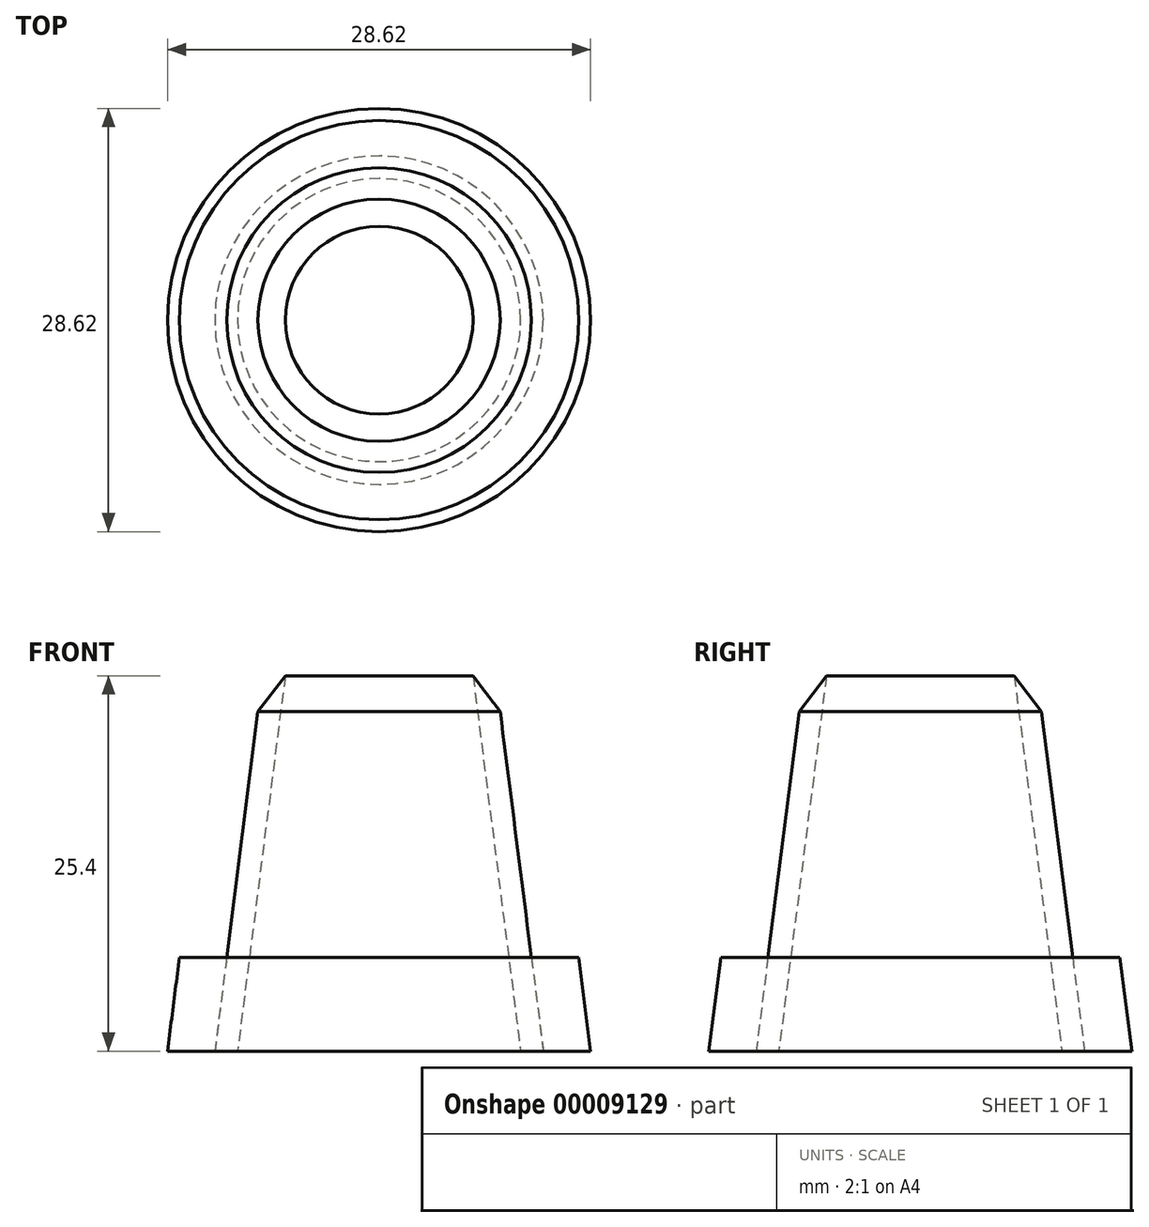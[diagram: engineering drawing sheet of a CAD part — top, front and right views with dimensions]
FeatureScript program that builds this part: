
annotation { "Feature Type Name" : "Feature", "Feature Type Description" : "" }
export const myFeature = defineFeature(function(context is Context, id is Id, definition is map)
    precondition{}
    {
        {
            var Q0;
            Q0=qCreatedBy(makeId("Front.planeOp"),FACE);
            var sketch = newSketch(context, id + "F0", { "sketchPlane" : qUnion([Q0])});
            skLineSegment(sketch, "E0", {"start": v(-11.11, 0) * mm, "end": v(-8.2, 22.97) * mm});
            skLineSegment(sketch, "E1", {"start": v(-6.35, 25.4) * mm, "end": v(-9.58, 0) * mm});
            skLineSegment(sketch, "E2", {"start": v(-9.58, 0) * mm, "end": v(-11.11, 0) * mm});
            skLineSegment(sketch, "E3", {"start": v(-6.35, 25.4) * mm, "end": v(-8.2, 22.97) * mm});
            skLineSegment(sketch, "E4", {"start": v(0, 23.24) * mm, "end": v(0, 5.77) * mm, "construction": true});
            skSolve(sketch);
        }
        {
            var Q0;
            Q0 = qSketchRegion(id + "F0", true);
            var Q1;
            Q1=sQuery(id+"F0.wireOp",EDGE,"E4");
            revolve(context, id + "F1", {"entities" : qUnion([Q0]), "axis" : qUnion([Q1]), "revolveType" : RevolveType.FULL});
        }
        {
            var Q0;
            Q0=qCreatedBy(makeId("Front.planeOp"),FACE);
            var sketch = newSketch(context, id + "F2", { "sketchPlane" : qUnion([Q0])});
            skLineSegment(sketch, "E5", {"start": v(-11.11, 0) * mm, "end": v(-10.3, 6.35) * mm});
            skLineSegment(sketch, "E6", {"start": v(-11.11, 0) * mm, "end": v(-14.31, 0) * mm});
            skLineSegment(sketch, "E7", {"start": v(-14.31, 0) * mm, "end": v(-13.5, 6.35) * mm});
            skLineSegment(sketch, "E8", {"start": v(-13.5, 6.35) * mm, "end": v(-10.3, 6.35) * mm});
            skLineSegment(sketch, "E9", {"start": v(-10.3, 6.35) * mm, "end": v(-11.11, 0) * mm});
            skLineSegment(sketch, "E10", {"start": v(0, 6.8) * mm, "end": v(0, 14.15) * mm, "construction": true});
            skSolve(sketch);
        }
        {
            var Q0;
            Q0=makeQuery(id+"F2.imprint","IMPRINT",FACE,{"disambiguationData":[TD([[makeQuery(id+"F2.imprint","IMPRINT",EDGE,{"derivedFrom":sQuery(id+"F2.wireOp",EDGE,"E6")}),-1.0]])]});
            var Q1;
            Q1=sQuery(id+"F2.wireOp",EDGE,"E10");
            revolve(context, id + "F3", {"entities" : qUnion([Q0]), "axis" : qUnion([Q1]), "revolveType" : RevolveType.FULL});
        }
    });
